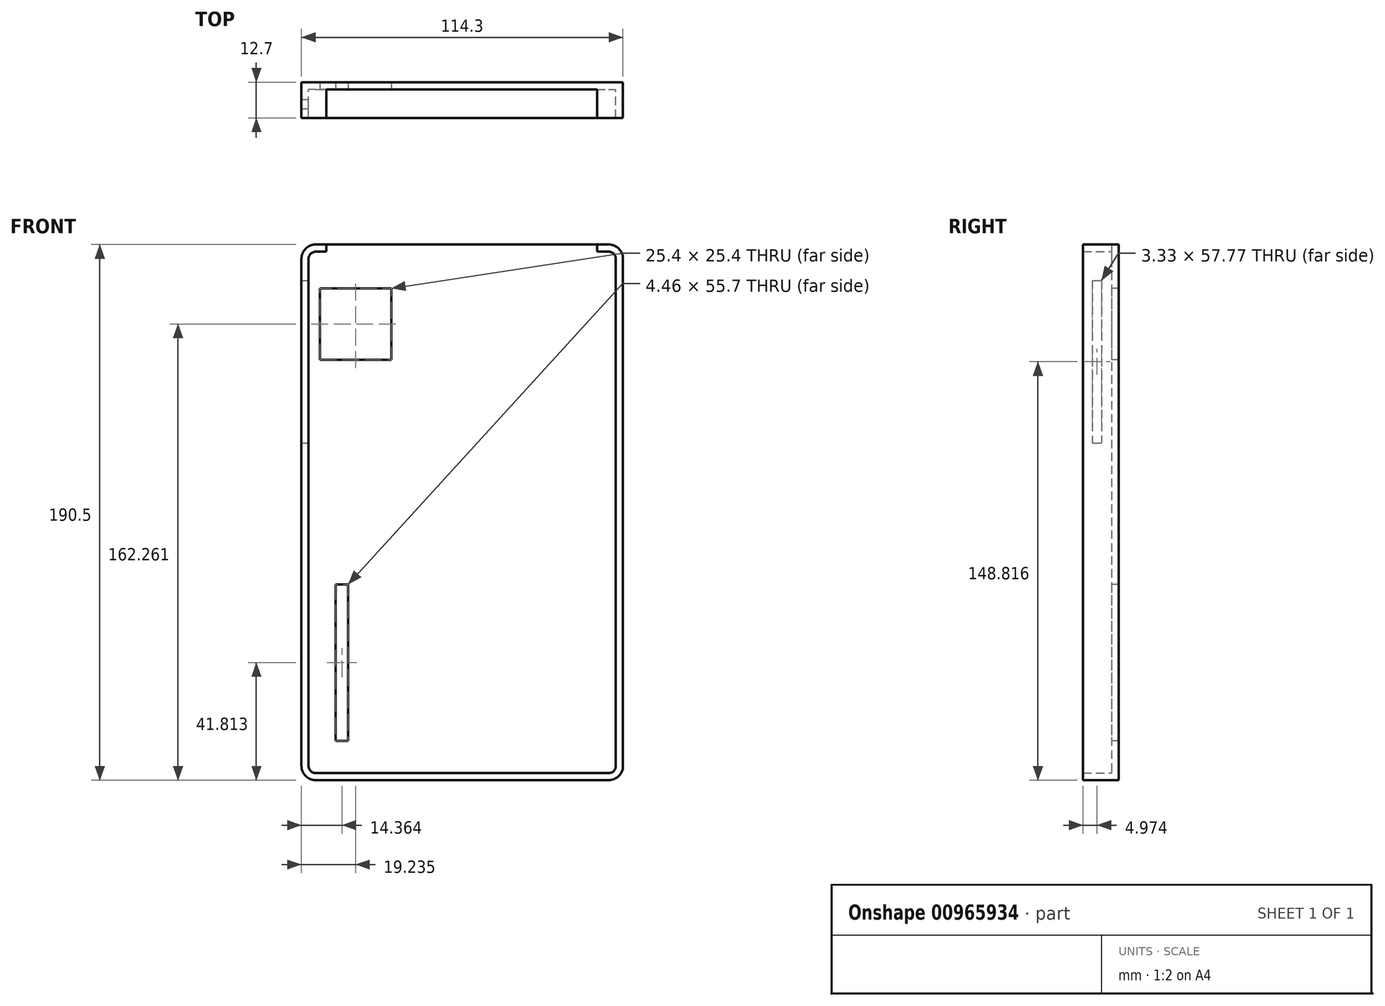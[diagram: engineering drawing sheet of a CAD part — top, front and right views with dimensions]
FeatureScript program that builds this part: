
annotation { "Feature Type Name" : "Feature", "Feature Type Description" : "" }
export const myFeature = defineFeature(function(context is Context, id is Id, definition is map)
    precondition{}
    {
        {
            var Q0;
            Q0=qCreatedBy(makeId("Front.planeOp"),FACE);
            var sketch = newSketch(context, id + "F0", { "sketchPlane" : qUnion([Q0])});
            skLineSegment(sketch, "E0.bottom", {"start": v(-50.47, 106.96) * mm, "end": v(63.83, 106.96) * mm});
            skLineSegment(sketch, "E0.top", {"start": v(-50.47, -83.54) * mm, "end": v(63.83, -83.54) * mm});
            skLineSegment(sketch, "E0.left", {"start": v(-50.47, 106.96) * mm, "end": v(-50.47, -83.54) * mm});
            skLineSegment(sketch, "E0.right", {"start": v(63.83, 106.96) * mm, "end": v(63.83, -83.54) * mm});
            skSolve(sketch);
        }
        {
            var Q0;
            Q0 = qSketchRegion(id + "F0", true);
            extrude(context, id + "F1", {"entities" : qUnion([Q0]), "depth" : 12.7 * mm, "offsetDistance" : 25.4 * mm});
        }
        {
            var Q0;
            Q0=makeQuery(id+"F1.opExtrude","SWEPT_EDGE",EDGE,{"disambiguationData":[OSD([sQuery(id+"F0.wireOp",EDGE,"E0.bottom"),sQuery(id+"F0.wireOp",EDGE,"E0.left")])]});
            var Q1;
            Q1=makeQuery(id+"F1.opExtrude","SWEPT_EDGE",EDGE,{"disambiguationData":[OSD([sQuery(id+"F0.wireOp",EDGE,"E0.top"),sQuery(id+"F0.wireOp",EDGE,"E0.left")])]});
            var Q2;
            Q2=makeQuery(id+"F1.opExtrude","SWEPT_EDGE",EDGE,{"disambiguationData":[OSD([sQuery(id+"F0.wireOp",EDGE,"E0.top"),sQuery(id+"F0.wireOp",EDGE,"E0.right")])]});
            var Q3;
            Q3=makeQuery(id+"F1.opExtrude","SWEPT_EDGE",EDGE,{"disambiguationData":[OSD([sQuery(id+"F0.wireOp",EDGE,"E0.bottom"),sQuery(id+"F0.wireOp",EDGE,"E0.right")])]});
            fillet(context, id + "F2", {"entities" : qUnion([Q0, Q1, Q2, Q3]), "tangentPropagation" : true, "radius" : 5.08 * mm, "defaultsChanged" : false, "vertexSettings" : [], "allowEdgeOverflow" : false});
        }
        {
            var Q0;
            Q0=makeQuery(id+"F1.opExtrude","CAP_FACE",FACE,{"disambiguationData":[OSD([sQuery(id+"F0.wireOp",EDGE,"E0.bottom"),sQuery(id+"F0.wireOp",EDGE,"E0.top"),sQuery(id+"F0.wireOp",EDGE,"E0.left"),sQuery(id+"F0.wireOp",EDGE,"E0.right")])],"isStart":false});
            shell(context, id + "F3", {"entities" : qUnion([Q0]), "thickness" : 2.54 * mm});
        }
        {
            var Q0;
            Q0=makeQuery(id+"F3.opShell","OFFSET_FACE",FACE,{"disambiguationData":[OSD([sQuery(id+"F0.wireOp",EDGE,"E0.bottom"),sQuery(id+"F0.wireOp",EDGE,"E0.top"),sQuery(id+"F0.wireOp",EDGE,"E0.left"),sQuery(id+"F0.wireOp",EDGE,"E0.right")])]});
            var sketch = newSketch(context, id + "F4", { "sketchPlane" : qUnion([Q0])});
            skLineSegment(sketch, "E1.bottom", {"start": v(-52.07, 94.6) * mm, "end": v(-56, 94.6) * mm});
            skLineSegment(sketch, "E1.top", {"start": v(-52.07, -8.97) * mm, "end": v(-56, -8.97) * mm});
            skLineSegment(sketch, "E1.left", {"start": v(-52.07, 94.6) * mm, "end": v(-52.07, -8.97) * mm});
            skLineSegment(sketch, "E1.right", {"start": v(-56, 94.6) * mm, "end": v(-56, -8.97) * mm});
            skLineSegment(sketch, "E2.bottom", {"start": v(-18.53, 91.42) * mm, "end": v(-43.93, 91.42) * mm});
            skLineSegment(sketch, "E2.top", {"start": v(-18.53, 66.02) * mm, "end": v(-43.93, 66.02) * mm});
            skLineSegment(sketch, "E2.left", {"start": v(-18.53, 91.42) * mm, "end": v(-18.53, 66.02) * mm});
            skLineSegment(sketch, "E2.right", {"start": v(-43.93, 91.42) * mm, "end": v(-43.93, 66.02) * mm});
            skSolve(sketch);
        }
        {
            var Q0;
            Q0 = qSketchRegion(id + "F4", true);
            extrude(context, id + "F5", {"entities" : qUnion([Q0]), "operationType" : NewBodyOperationType.REMOVE, "endBound" : BoundingType.THROUGH_ALL, "oppositeDirection" : true, "depth" : 25.4 * mm, "offsetDistance" : 25.4 * mm});
        }
        {
            var Q0;
            Q0=makeQuery(id+"F3.opShell","OFFSET_FACE",FACE,{"disambiguationData":[OSD([sQuery(id+"F0.wireOp",EDGE,"E0.left")])]});
            var sketch = newSketch(context, id + "F6", { "sketchPlane" : qUnion([Q0])});
            skLineSegment(sketch, "E3.bottom", {"start": v(-9.4, 94.16) * mm, "end": v(-6.06, 94.16) * mm});
            skLineSegment(sketch, "E3.top", {"start": v(-9.4, 36.39) * mm, "end": v(-6.06, 36.39) * mm});
            skLineSegment(sketch, "E3.left", {"start": v(-9.4, 94.16) * mm, "end": v(-9.4, 36.39) * mm});
            skLineSegment(sketch, "E3.right", {"start": v(-6.06, 94.16) * mm, "end": v(-6.06, 36.39) * mm});
            skSolve(sketch);
        }
        {
            var Q0;
            Q0 = qSketchRegion(id + "F6", true);
            extrude(context, id + "F7", {"entities" : qUnion([Q0]), "operationType" : NewBodyOperationType.REMOVE, "endBound" : BoundingType.THROUGH_ALL, "oppositeDirection" : true, "depth" : 25.4 * mm, "offsetDistance" : 25.4 * mm});
        }
        {
            var Q0;
            Q0 = qSketchRegion(id + "F4", true);
            extrude(context, id + "F8", {"entities" : qUnion([Q0]), "operationType" : NewBodyOperationType.REMOVE, "endBound" : BoundingType.THROUGH_ALL, "oppositeDirection" : true, "depth" : 25.4 * mm, "offsetDistance" : 25.4 * mm});
        }
        {
            var Q0;
            Q0=makeQuery(id+"F3.opShell","OFFSET_FACE",FACE,{"disambiguationData":[OSD([sQuery(id+"F0.wireOp",EDGE,"E0.bottom")])]});
            var sketch = newSketch(context, id + "F9", { "sketchPlane" : qUnion([Q0])});
            skLineSegment(sketch, "E4.bottom", {"start": v(-41.6, 12.7) * mm, "end": v(54.62, 12.7) * mm});
            skLineSegment(sketch, "E4.top", {"start": v(-41.6, 2.54) * mm, "end": v(54.62, 2.54) * mm});
            skLineSegment(sketch, "E4.left", {"start": v(-41.6, 12.7) * mm, "end": v(-41.6, 2.54) * mm});
            skLineSegment(sketch, "E4.right", {"start": v(54.62, 12.7) * mm, "end": v(54.62, 2.54) * mm});
            skSolve(sketch);
        }
        {
            var Q0;
            Q0 = qSketchRegion(id + "F9", true);
            extrude(context, id + "F10", {"entities" : qUnion([Q0]), "operationType" : NewBodyOperationType.REMOVE, "endBound" : BoundingType.THROUGH_ALL, "oppositeDirection" : true, "depth" : 25.4 * mm, "offsetDistance" : 25.4 * mm});
        }
        {
            var Q0;
            Q0=makeQuery(id+"F10.boolean.opBoolean","MERGE",FACE,{"derivedFrom":[makeQuery(id+"F3.opShell","OFFSET_FACE",FACE,{"disambiguationData":[OSD([sQuery(id+"F0.wireOp",EDGE,"E0.bottom"),sQuery(id+"F0.wireOp",EDGE,"E0.top"),sQuery(id+"F0.wireOp",EDGE,"E0.left"),sQuery(id+"F0.wireOp",EDGE,"E0.right")])]})],"fromTools":[makeQuery(id+"F10.opExtrude","SWEPT_FACE",FACE,{"disambiguationData":[OSD([sQuery(id+"F9.wireOp",EDGE,"E4.top")])]})]});
            var sketch = newSketch(context, id + "F11", { "sketchPlane" : qUnion([Q0])});
            skLineSegment(sketch, "E5.bottom", {"start": v(-38.33, -13.88) * mm, "end": v(-33.88, -13.88) * mm});
            skLineSegment(sketch, "E5.top", {"start": v(-38.33, -69.57) * mm, "end": v(-33.88, -69.57) * mm});
            skLineSegment(sketch, "E5.left", {"start": v(-38.33, -13.88) * mm, "end": v(-38.33, -69.57) * mm});
            skLineSegment(sketch, "E5.right", {"start": v(-33.88, -13.88) * mm, "end": v(-33.88, -69.57) * mm});
            skSolve(sketch);
        }
        {
            var Q0;
            Q0 = qSketchRegion(id + "F11", true);
            extrude(context, id + "F12", {"entities" : qUnion([Q0]), "operationType" : NewBodyOperationType.REMOVE, "endBound" : BoundingType.THROUGH_ALL, "oppositeDirection" : true, "depth" : 25.4 * mm, "offsetDistance" : 25.4 * mm});
        }
    });
